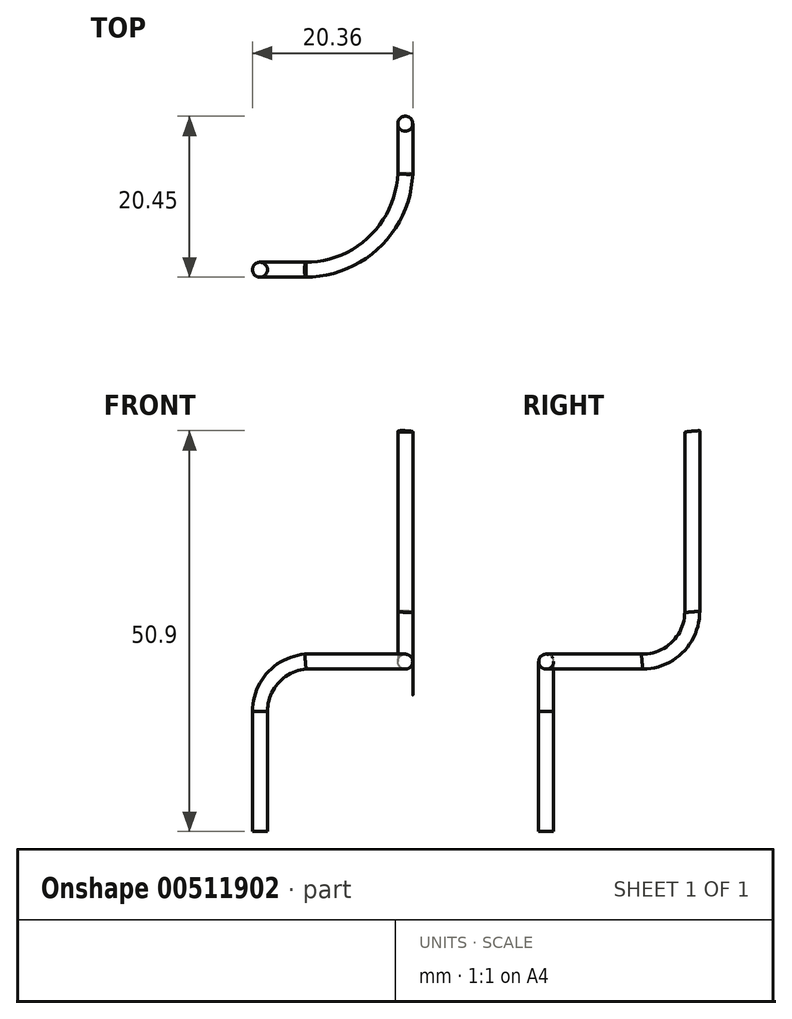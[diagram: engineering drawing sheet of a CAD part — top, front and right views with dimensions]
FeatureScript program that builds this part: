
annotation { "Feature Type Name" : "Feature", "Feature Type Description" : "" }
export const myFeature = defineFeature(function(context is Context, id is Id, definition is map)
    precondition{}
    {
        {
            var Q0;
            Q0=qCreatedBy(makeId("Top.planeOp"),FACE);
            var sketch = newSketch(context, id + "F0", { "sketchPlane" : qUnion([Q0])});
            skCircle(sketch, "E0", {"center": v(0, 0) * mm, "radius": 0.95 * mm});
            skSolve(sketch);
        }
        {
            var Q0;
            Q0=qCreatedBy(makeId("Front.planeOp"),FACE);
            var sketch = newSketch(context, id + "F1", { "sketchPlane" : qUnion([Q0])});
            skLineSegment(sketch, "E1", {"start": v(0, 0) * mm, "end": v(0, 15.24) * mm});
            skArc(sketch, "E2", {"start": v(5.76, 21.56) * mm, "mid": v(1.66, 19.52) * mm, "end": v(0, 15.24) * mm});
            skSolve(sketch);
        }
        {
            var Q0;
            Q0=qCreatedBy(makeId("Top.planeOp"),FACE);
            var Q1;
            Q1=sQuery(id+"F1.wireOp",VERTEX,"E2.start");
            cPlane(context, id + "F2", {"entities" : qUnion([Q0, Q1]), "cplaneType" : CPlaneType.PLANE_POINT, "offset" : 17.78 * mm, "width" : 152.4 * mm, "height" : 152.4 * mm});
        }
        {
            var Q0;
            Q0=qCreatedBy(id+"F2.planeOp",FACE);
            var sketch = newSketch(context, id + "F3", { "sketchPlane" : qUnion([Q0])});
            skArc(sketch, "E3", {"start": v(5.76, 0) * mm, "mid": v(14.57, 3.55) * mm, "end": v(18.45, 12.2) * mm});
            skSolve(sketch);
        }
        {
            var Q0;
            Q0=sQuery(id+"F3.wireOp",VERTEX,"E3.end");
            var Q1;
            Q1=qCreatedBy(makeId("Right.planeOp"),FACE);
            cPlane(context, id + "F4", {"entities" : qUnion([Q0, Q1]), "cplaneType" : CPlaneType.PLANE_POINT, "offset" : 25.4 * mm, "width" : 152.4 * mm, "height" : 152.4 * mm});
        }
        {
            var Q0;
            Q0=qCreatedBy(id+"F4.planeOp",FACE);
            var sketch = newSketch(context, id + "F5", { "sketchPlane" : qUnion([Q0])});
            skArc(sketch, "E4", {"start": v(12.2, 21.56) * mm, "mid": v(16.7, 23.42) * mm, "end": v(18.56, 27.91) * mm});
            skLineSegment(sketch, "E5", {"start": v(18.56, 27.91) * mm, "end": v(18.56, 50.8) * mm});
            skSolve(sketch);
        }
        {
            var Q0;
            Q0=makeQuery(id+"F0.imprint","IMPRINT",FACE,{"disambiguationData":[TD([[makeQuery(id+"F0.imprint","IMPRINT",EDGE,{"derivedFrom":sQuery(id+"F0.wireOp",EDGE,"E0")}),1.0]])]});
            var Q1;
            Q1=sQuery(id+"F1.wireOp",EDGE,"E1");
            sweep(context, id + "F6", {"profiles" : qUnion([Q0]), "path" : qUnion([Q1])});
        }
        {
            var Q0;
            Q0=makeQuery(id+"F6.opSweep","CAP_FACE",FACE,{"disambiguationData":[OSD([sQuery(id+"F0.wireOp",EDGE,"E0"),sQuery(id+"F1.wireOp",VERTEX,"E1.end")])],"isStart":false});
            var Q1;
            Q1=makeQuery(id+"F6.opSweep","CAP_EDGE",EDGE,{"disambiguationData":[OSD([sQuery(id+"F0.wireOp",EDGE,"E0"),sQuery(id+"F1.wireOp",VERTEX,"E1.end")])],"isStart":false});
            var Q2;
            Q2=sQuery(id+"F1.wireOp",EDGE,"E2");
            sweep(context, id + "F7", {"profiles" : qUnion([Q0]), "surfaceProfiles" : qUnion([Q1]), "path" : qUnion([Q2])});
        }
        {
            var Q0;
            Q0=makeQuery(id+"F7.opSweep","CAP_FACE",FACE,{"disambiguationData":[OSD([sQuery(id+"F0.wireOp",EDGE,"E0"),sQuery(id+"F1.wireOp",VERTEX,"E1.end"),sQuery(id+"F1.wireOp",VERTEX,"E2.start")])],"isStart":false});
            var Q1;
            Q1=makeQuery(id+"F7.opSweep","CAP_EDGE",EDGE,{"disambiguationData":[OSD([sQuery(id+"F0.wireOp",EDGE,"E0"),sQuery(id+"F1.wireOp",VERTEX,"E1.end"),sQuery(id+"F1.wireOp",VERTEX,"E2.start")])],"isStart":false});
            var Q2;
            Q2=sQuery(id+"F3.wireOp",EDGE,"E3");
            sweep(context, id + "F8", {"profiles" : qUnion([Q0]), "surfaceProfiles" : qUnion([Q1]), "path" : qUnion([Q2])});
        }
        {
            var Q0;
            Q0=makeQuery(id+"F8.opSweep","CAP_FACE",FACE,{"disambiguationData":[OSD([sQuery(id+"F0.wireOp",EDGE,"E0"),sQuery(id+"F1.wireOp",VERTEX,"E1.end"),sQuery(id+"F1.wireOp",VERTEX,"E2.start"),sQuery(id+"F3.wireOp",VERTEX,"E3.end")])],"isStart":false});
            var Q1;
            Q1=sQuery(id+"F5.wireOp",EDGE,"E4");
            sweep(context, id + "F9", {"operationType" : NewBodyOperationType.ADD, "profiles" : qUnion([Q0]), "path" : qUnion([Q1])});
        }
        {
            var Q0;
            Q0=makeQuery(id+"F9.opSweep","CAP_FACE",FACE,{"disambiguationData":[OSD([sQuery(id+"F0.wireOp",EDGE,"E0"),sQuery(id+"F1.wireOp",VERTEX,"E1.end"),sQuery(id+"F1.wireOp",VERTEX,"E2.start"),sQuery(id+"F3.wireOp",VERTEX,"E3.end"),sQuery(id+"F5.wireOp",VERTEX,"E4.end")])],"isStart":false});
            var Q1;
            Q1=sQuery(id+"F5.wireOp",EDGE,"E5");
            sweep(context, id + "F10", {"operationType" : NewBodyOperationType.ADD, "profiles" : qUnion([Q0]), "path" : qUnion([Q1])});
        }
    });
